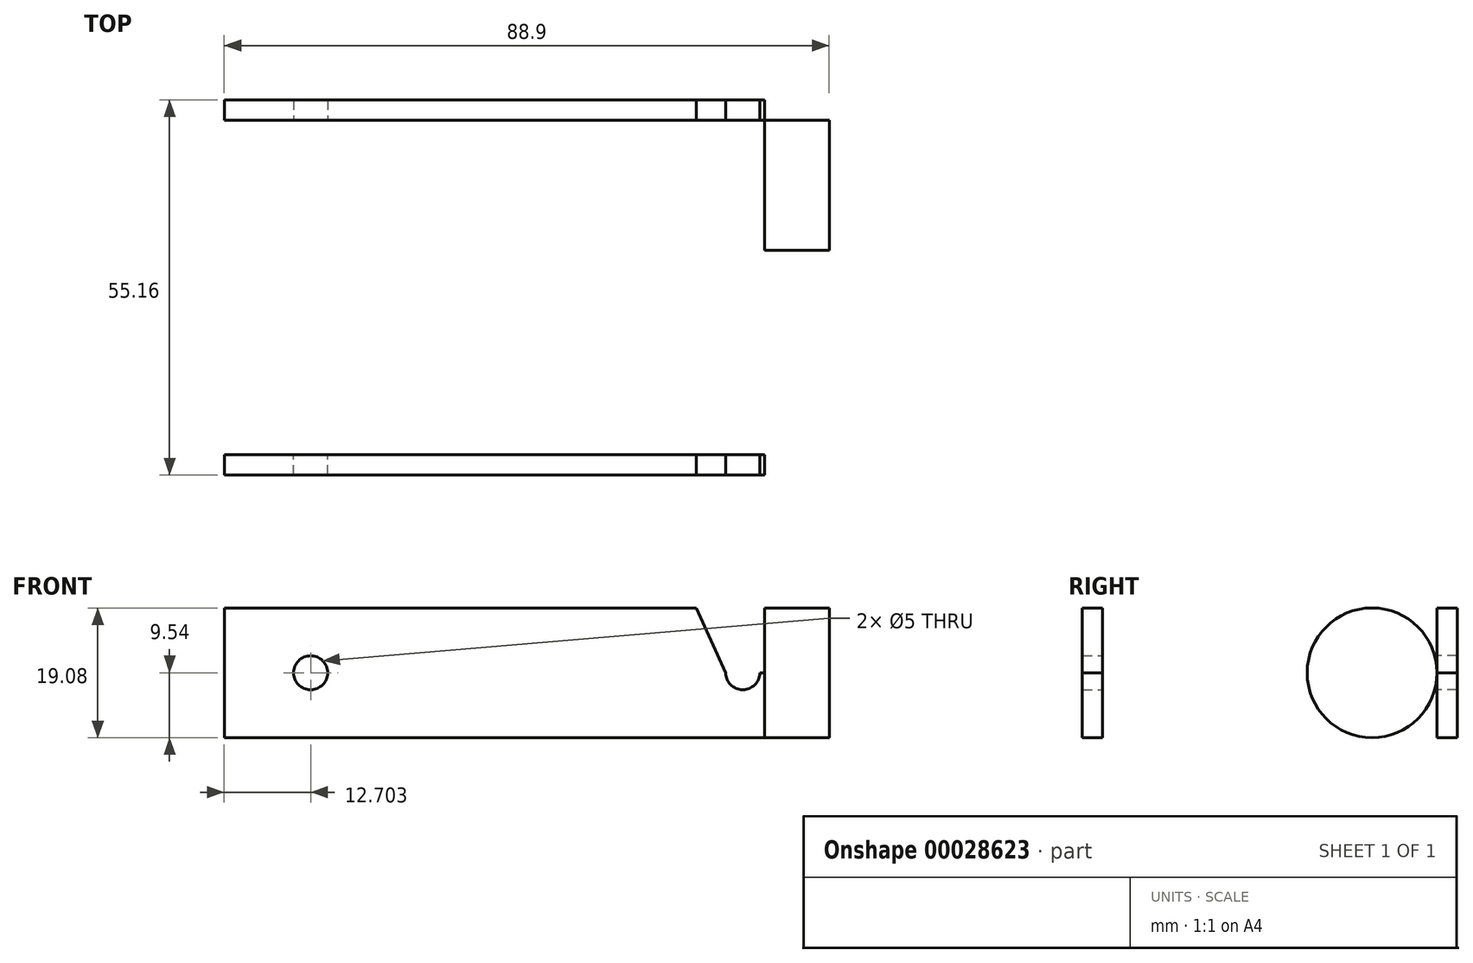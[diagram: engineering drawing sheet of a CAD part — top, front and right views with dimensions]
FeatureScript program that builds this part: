
annotation { "Feature Type Name" : "Feature", "Feature Type Description" : "" }
export const myFeature = defineFeature(function(context is Context, id is Id, definition is map)
    precondition{}
    {
        {
            var Q0;
            Q0=qCreatedBy(makeId("Right.planeOp"),FACE);
            var sketch = newSketch(context, id + "F0", { "sketchPlane" : qUnion([Q0])});
            skLineSegment(sketch, "E0.rect.bottom", {"start": v(31.75, -19.05) * mm, "end": v(-31.75, -19.05) * mm});
            skLineSegment(sketch, "E0.rect.top", {"start": v(31.75, 19.05) * mm, "end": v(-31.75, 19.05) * mm});
            skLineSegment(sketch, "E0.rect.left", {"start": v(31.75, -19.05) * mm, "end": v(31.75, 19.05) * mm});
            skLineSegment(sketch, "E0.rect.right", {"start": v(-31.75, -19.05) * mm, "end": v(-31.75, 19.05) * mm});
            skPoint(sketch, "E0.rect.middle", {"position": v(0, 0) * mm});
            skSolve(sketch);
        }
        {
            var Q0;
            Q0=makeQuery(id+"F0.imprint","IMPRINT",FACE,{"disambiguationData":[TD([[makeQuery(id+"F0.imprint","IMPRINT",EDGE,{"derivedFrom":sQuery(id+"F0.wireOp",EDGE,"E0.rect.bottom")}),-1.0]])]});
            extrude(context, id + "F1", {"entities" : qUnion([Q0]), "endBound" : BoundingType.SYMMETRIC, "depth" : 9.52 * mm});
        }
        {
            var Q0;
            Q0=makeQuery(id+"F1.opExtrude","CAP_FACE",FACE,{"disambiguationData":[OSD([sQuery(id+"F0.wireOp",EDGE,"E0.rect.bottom"),sQuery(id+"F0.wireOp",EDGE,"E0.rect.top"),sQuery(id+"F0.wireOp",EDGE,"E0.rect.left"),sQuery(id+"F0.wireOp",EDGE,"E0.rect.right")])],"isStart":false});
            var sketch = newSketch(context, id + "F2", { "sketchPlane" : qUnion([Q0])});
            skCircle(sketch, "E1", {"center": v(-15.04, 0) * mm, "radius": 9.54 * mm});
            skLineSegment(sketch, "E2.bottom", {"start": v(-24.58, 0) * mm, "end": v(-5.5, 0) * mm});
            skLineSegment(sketch, "E2.top", {"start": v(-24.58, 19.05) * mm, "end": v(-5.5, 19.05) * mm});
            skLineSegment(sketch, "E2.left", {"start": v(-24.58, 0) * mm, "end": v(-24.58, 19.05) * mm});
            skLineSegment(sketch, "E2.right", {"start": v(-5.5, 0) * mm, "end": v(-5.5, 19.05) * mm});
            skLineSegment(sketch, "E3.MirrorCS", {"start": v(5.5, 0) * mm, "end": v(5.5, 19.05) * mm});
            skLineSegment(sketch, "E4.MirrorCS", {"start": v(24.58, 0) * mm, "end": v(24.58, 19.05) * mm});
            skLineSegment(sketch, "E5.MirrorCS", {"start": v(24.58, 19.05) * mm, "end": v(5.5, 19.05) * mm});
            skCircle(sketch, "E6.MirrorC", {"center": v(15.04, 0) * mm, "radius": 9.54 * mm});
            skSolve(sketch);
        }
        {
            var Q0;
            Q0=makeQuery(id+"F2.imprint","IMPRINT",FACE,{"disambiguationData":[TD([[makeQuery(id+"F2.imprint","IMPRINT",EDGE,{"derivedFrom":sQuery(id+"F2.wireOp",EDGE,"E2.top")}),1.0]])]});
            var Q1;
            {var subQ0=sQuery(id+"F2.wireOp",EDGE,"E2.bottom");Q1=makeQuery(id+"F2.imprint","IMPRINT",FACE,{"disambiguationData":[TD([[makeQuery(id+"F2.imprint","IMPRINT",EDGE,{"derivedFrom":subQ0}),1.0]])]});}
            var Q2;
            {var subQ0=sQuery(id+"F2.wireOp",EDGE,"E2.bottom");Q2=makeQuery(id+"F2.imprint","IMPRINT",FACE,{"disambiguationData":[TD([[makeQuery(id+"F2.imprint","IMPRINT",EDGE,{"derivedFrom":subQ0}),-1.0]])]});}
            var Q3;
            {var subQ0=sQuery(id+"F2.wireOp",EDGE,"E6.MirrorC");var subQ2=makeQuery(id+"F2.imprint","INTERSECT",VERTEX,{"derivedFrom":[sQuery(id+"F2.wireOp",EDGE,"E3.MirrorCS"),subQ0]});Q3=makeQuery(id+"F2.imprint","IMPRINT",FACE,{"disambiguationData":[TD([[makeQuery(id+"F2.imprint","IMPRINT",EDGE,{"disambiguationData":[TD([[subQ2,-1.0]])],"derivedFrom":subQ0}),-1.0]])]});}
            var Q4;
            {var subQ2=sQuery(id+"F2.wireOp",EDGE,"E3.MirrorCS");Q4=makeQuery(id+"F2.imprint","IMPRINT",FACE,{"disambiguationData":[TD([[makeQuery(id+"F2.imprint","IMPRINT",EDGE,{"derivedFrom":subQ2}),-1.0]])]});}
            extrude(context, id + "F3", {"entities" : qUnion([Q0, Q1, Q2, Q3, Q4]), "operationType" : NewBodyOperationType.REMOVE, "oppositeDirection" : true, "depth" : 9.52 * mm});
        }
        {
            var Q0;
            Q0=makeQuery(id+"F1.opExtrude","CAP_FACE",FACE,{"disambiguationData":[OSD([sQuery(id+"F0.wireOp",EDGE,"E0.rect.bottom"),sQuery(id+"F0.wireOp",EDGE,"E0.rect.top"),sQuery(id+"F0.wireOp",EDGE,"E0.rect.left"),sQuery(id+"F0.wireOp",EDGE,"E0.rect.right")])],"isStart":true});
            var sketch = newSketch(context, id + "F4", { "sketchPlane" : qUnion([Q0])});
            skLineSegment(sketch, "E7.bottom", {"start": v(27.58, -9.54) * mm, "end": v(24.58, -9.54) * mm});
            skLineSegment(sketch, "E7.top", {"start": v(27.58, 9.54) * mm, "end": v(24.58, 9.54) * mm});
            skLineSegment(sketch, "E7.left", {"start": v(27.58, -9.54) * mm, "end": v(27.58, 9.54) * mm});
            skLineSegment(sketch, "E7.right", {"start": v(24.58, -9.54) * mm, "end": v(24.58, 9.54) * mm});
            skPoint(sketch, "E8", {"position": v(15.04, -9.54) * mm});
            skPoint(sketch, "E9", {"position": v(15.21, -9.64) * mm});
            skLineSegment(sketch, "E10.MirrorCS", {"start": v(-27.58, 9.54) * mm, "end": v(-24.58, 9.54) * mm});
            skLineSegment(sketch, "E11.MirrorCS", {"start": v(-27.58, -9.54) * mm, "end": v(-27.58, 9.54) * mm});
            skLineSegment(sketch, "E12.MirrorCS", {"start": v(-24.58, -9.54) * mm, "end": v(-24.58, 9.54) * mm});
            skLineSegment(sketch, "E13.MirrorCS", {"start": v(-27.58, -9.54) * mm, "end": v(-24.58, -9.54) * mm});
            skSolve(sketch);
        }
        {
            var Q0;
            {var subQ2=sQuery(id+"F4.wireOp",EDGE,"E10.MirrorCS");Q0=makeQuery(id+"F4.imprint","IMPRINT",FACE,{"disambiguationData":[TD([[makeQuery(id+"F4.imprint","IMPRINT",EDGE,{"derivedFrom":subQ2}),-1.0]])]});}
            var Q1;
            {var subQ3=sQuery(id+"F4.wireOp",EDGE,"E7.bottom");Q1=makeQuery(id+"F4.imprint","IMPRINT",FACE,{"disambiguationData":[TD([[makeQuery(id+"F4.imprint","IMPRINT",EDGE,{"derivedFrom":subQ3}),-1.0]])]});}
            extrude(context, id + "F5", {"entities" : qUnion([Q0, Q1]), "operationType" : NewBodyOperationType.ADD, "depth" : 76.2 * mm + 12.7 * mm - 9.52 * mm});
        }
        {
            var Q0;
            Q0=makeQuery(id+"F5.boolean.opBoolean","MERGE",FACE,{"derivedFrom":[makeQuery(id+"F3.boolean.opBoolean","COPY",FACE,{"derivedFrom":makeQuery(id+"F3.opExtrude","SWEPT_FACE",FACE,{"disambiguationData":[OSD([sQuery(id+"F2.wireOp",EDGE,"E4.MirrorCS")])]})}),makeQuery(id+"F5.opExtrude","SWEPT_FACE",FACE,{"disambiguationData":[OSD([sQuery(id+"F4.wireOp",EDGE,"E12.MirrorCS")])]})]});
            var sketch = newSketch(context, id + "F6", { "sketchPlane" : qUnion([Q0])});
            skCircle(sketch, "E14", {"center": v(-71.44, 0) * mm, "radius": 2.5 * mm});
            skSolve(sketch);
        }
        {
            var Q0;
            Q0=makeQuery(id+"F6.imprint","IMPRINT",FACE,{"disambiguationData":[TD([[makeQuery(id+"F6.imprint","IMPRINT",EDGE,{"derivedFrom":sQuery(id+"F6.wireOp",EDGE,"E14")}),1.0]])]});
            var Q1;
            Q1=makeQuery(id+"F5.opExtrude","SWEPT_FACE",FACE,{"disambiguationData":[OSD([sQuery(id+"F4.wireOp",EDGE,"E11.MirrorCS")])]});
            extrude(context, id + "F7", {"entities" : qUnion([Q0]), "operationType" : NewBodyOperationType.REMOVE, "endBound" : BoundingType.UP_TO_SURFACE, "oppositeDirection" : true, "endBoundEntityFace" : qUnion([Q1]), "depth" : 25.4 * mm, "hasSecondDirection" : true, "secondDirectionOppositeDirection" : false, "secondDirectionDepth" : 25.4 * mm});
        }
        {
            var Q0;
            Q0=makeQuery(id+"F5.boolean.opBoolean","MERGE",FACE,{"derivedFrom":[makeQuery(id+"F3.boolean.opBoolean","COPY",FACE,{"derivedFrom":makeQuery(id+"F3.opExtrude","SWEPT_FACE",FACE,{"disambiguationData":[OSD([sQuery(id+"F2.wireOp",EDGE,"E2.left")])]})}),makeQuery(id+"F5.opExtrude","SWEPT_FACE",FACE,{"disambiguationData":[OSD([sQuery(id+"F4.wireOp",EDGE,"E7.right")])]})]});
            var sketch = newSketch(context, id + "F8", { "sketchPlane" : qUnion([Q0])});
            skCircle(sketch, "E15", {"center": v(71.44, 0) * mm, "radius": 2.5 * mm});
            skSolve(sketch);
        }
        {
            var Q0;
            Q0=makeQuery(id+"F8.imprint","IMPRINT",FACE,{"disambiguationData":[TD([[makeQuery(id+"F8.imprint","IMPRINT",EDGE,{"derivedFrom":sQuery(id+"F8.wireOp",EDGE,"E15")}),1.0]])]});
            var Q1;
            Q1=makeQuery(id+"F5.opExtrude","SWEPT_FACE",FACE,{"disambiguationData":[OSD([sQuery(id+"F4.wireOp",EDGE,"E7.left")])]});
            extrude(context, id + "F9", {"entities" : qUnion([Q0]), "operationType" : NewBodyOperationType.REMOVE, "endBound" : BoundingType.UP_TO_SURFACE, "oppositeDirection" : true, "endBoundEntityFace" : qUnion([Q1]), "depth" : 25.4 * mm});
        }
        {
            var Q0;
            Q0=makeQuery(id+"F5.boolean.opBoolean","MERGE",FACE,{"derivedFrom":[makeQuery(id+"F3.boolean.opBoolean","COPY",FACE,{"derivedFrom":makeQuery(id+"F3.opExtrude","SWEPT_FACE",FACE,{"disambiguationData":[OSD([sQuery(id+"F2.wireOp",EDGE,"E4.MirrorCS")])]})}),makeQuery(id+"F5.opExtrude","SWEPT_FACE",FACE,{"disambiguationData":[OSD([sQuery(id+"F4.wireOp",EDGE,"E12.MirrorCS")])]})]});
            var sketch = newSketch(context, id + "F10", { "sketchPlane" : qUnion([Q0])});
            skLineSegment(sketch, "E16.bottom", {"start": v(-4.76, 0) * mm, "end": v(-14.76, 0) * mm});
            skLineSegment(sketch, "E16.top", {"start": v(-4.76, 9.54) * mm, "end": v(-14.76, 9.54) * mm});
            skLineSegment(sketch, "E16.left", {"start": v(-4.76, 0) * mm, "end": v(-4.76, 9.54) * mm});
            skLineSegment(sketch, "E16.right", {"start": v(-14.76, 0) * mm, "end": v(-14.76, 9.54) * mm});
            skCircle(sketch, "E17", {"center": v(-7.94, 0) * mm, "radius": 2.5 * mm});
            skLineSegment(sketch, "E18", {"start": v(-14.76, 9.54) * mm, "end": v(-10.44, 0) * mm});
            skSolve(sketch);
        }
        {
            var Q0;
            Q0=makeQuery(id+"F10.imprint","IMPRINT",FACE,{"disambiguationData":[TD([[makeQuery(id+"F10.imprint","IMPRINT",EDGE,{"derivedFrom":sQuery(id+"F10.wireOp",EDGE,"E16.top")}),-1.0]])]});
            var Q1;
            {var subQ0=sQuery(id+"F10.wireOp",EDGE,"E17");var subQ1=sQuery(id+"F10.wireOp",EDGE,"E16.bottom");var subQ2=makeQuery(id+"F10.imprint","INTERSECT",VERTEX,{"derivedFrom":[subQ1,subQ0]});Q1=makeQuery(id+"F10.imprint","IMPRINT",FACE,{"disambiguationData":[TD([[makeQuery(id+"F10.imprint","IMPRINT",EDGE,{"disambiguationData":[TD([[subQ2,-1.0]])],"derivedFrom":subQ1}),-1.0]])]});}
            var Q2;
            {var subQ0=sQuery(id+"F10.wireOp",EDGE,"E17");var subQ1=sQuery(id+"F10.wireOp",EDGE,"E16.bottom");var subQ2=makeQuery(id+"F10.imprint","INTERSECT",VERTEX,{"derivedFrom":[subQ1,subQ0]});Q2=makeQuery(id+"F10.imprint","IMPRINT",FACE,{"disambiguationData":[TD([[makeQuery(id+"F10.imprint","IMPRINT",EDGE,{"disambiguationData":[TD([[subQ2,-1.0]])],"derivedFrom":subQ1}),1.0]])]});}
            var Q3;
            Q3=makeQuery(id+"F5.opExtrude","SWEPT_FACE",FACE,{"disambiguationData":[OSD([sQuery(id+"F4.wireOp",EDGE,"E11.MirrorCS")])]});
            extrude(context, id + "F11", {"entities" : qUnion([Q0, Q1, Q2]), "operationType" : NewBodyOperationType.REMOVE, "endBound" : BoundingType.UP_TO_SURFACE, "oppositeDirection" : true, "endBoundEntityFace" : qUnion([Q3]), "depth" : 25.4 * mm});
        }
        {
            var Q0;
            Q0=makeQuery(id+"F5.boolean.opBoolean","MERGE",FACE,{"derivedFrom":[makeQuery(id+"F3.boolean.opBoolean","COPY",FACE,{"derivedFrom":makeQuery(id+"F3.opExtrude","SWEPT_FACE",FACE,{"disambiguationData":[OSD([sQuery(id+"F2.wireOp",EDGE,"E2.left")])]})}),makeQuery(id+"F5.opExtrude","SWEPT_FACE",FACE,{"disambiguationData":[OSD([sQuery(id+"F4.wireOp",EDGE,"E7.right")])]})]});
            var sketch = newSketch(context, id + "F12", { "sketchPlane" : qUnion([Q0])});
            skLineSegment(sketch, "E19.bottom", {"start": v(4.76, 0) * mm, "end": v(14.76, 0) * mm});
            skLineSegment(sketch, "E19.top", {"start": v(4.76, 9.54) * mm, "end": v(14.76, 9.54) * mm});
            skLineSegment(sketch, "E19.left", {"start": v(4.76, 0) * mm, "end": v(4.76, 9.54) * mm});
            skLineSegment(sketch, "E19.right", {"start": v(14.76, 0) * mm, "end": v(14.76, 9.54) * mm});
            skCircle(sketch, "E20", {"center": v(7.94, 0) * mm, "radius": 2.5 * mm});
            skLineSegment(sketch, "E21", {"start": v(14.76, 9.54) * mm, "end": v(10.44, 0) * mm});
            skSolve(sketch);
        }
        {
            var Q0;
            Q0=makeQuery(id+"F12.imprint","IMPRINT",FACE,{"disambiguationData":[TD([[makeQuery(id+"F12.imprint","IMPRINT",EDGE,{"derivedFrom":sQuery(id+"F12.wireOp",EDGE,"E19.top")}),1.0]])]});
            var Q1;
            {var subQ0=sQuery(id+"F12.wireOp",EDGE,"E20");var subQ1=sQuery(id+"F12.wireOp",EDGE,"E19.bottom");var subQ2=makeQuery(id+"F12.imprint","INTERSECT",VERTEX,{"derivedFrom":[subQ1,subQ0]});Q1=makeQuery(id+"F12.imprint","IMPRINT",FACE,{"disambiguationData":[TD([[makeQuery(id+"F12.imprint","IMPRINT",EDGE,{"disambiguationData":[TD([[subQ2,-1.0]])],"derivedFrom":subQ1}),1.0]])]});}
            var Q2;
            {var subQ0=sQuery(id+"F12.wireOp",EDGE,"E20");var subQ1=sQuery(id+"F12.wireOp",EDGE,"E19.bottom");var subQ2=makeQuery(id+"F12.imprint","INTERSECT",VERTEX,{"derivedFrom":[subQ1,subQ0]});Q2=makeQuery(id+"F12.imprint","IMPRINT",FACE,{"disambiguationData":[TD([[makeQuery(id+"F12.imprint","IMPRINT",EDGE,{"disambiguationData":[TD([[subQ2,-1.0]])],"derivedFrom":subQ1}),-1.0]])]});}
            var Q3;
            Q3=makeQuery(id+"F5.opExtrude","SWEPT_FACE",FACE,{"disambiguationData":[OSD([sQuery(id+"F4.wireOp",EDGE,"E7.left")])]});
            extrude(context, id + "F13", {"entities" : qUnion([Q0, Q1, Q2]), "operationType" : NewBodyOperationType.REMOVE, "endBound" : BoundingType.UP_TO_SURFACE, "oppositeDirection" : true, "endBoundEntityFace" : qUnion([Q3]), "depth" : 25.4 * mm});
        }
    });
